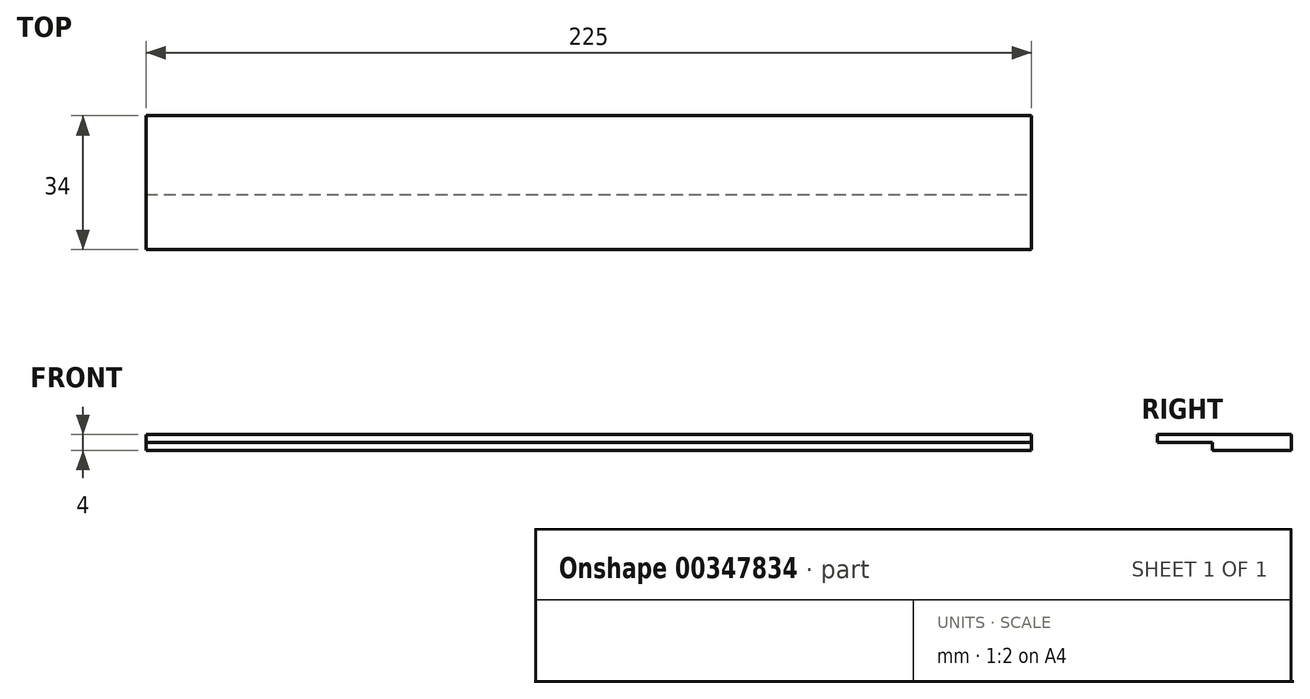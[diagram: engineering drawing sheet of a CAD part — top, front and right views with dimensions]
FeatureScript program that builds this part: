
annotation { "Feature Type Name" : "Feature", "Feature Type Description" : "" }
export const myFeature = defineFeature(function(context is Context, id is Id, definition is map)
    precondition{}
    {
        {
            var Q0;
            Q0=qCreatedBy(makeId("Top.planeOp"),FACE);
            var sketch = newSketch(context, id + "F0", { "sketchPlane" : qUnion([Q0])});
            skLineSegment(sketch, "E0.bottom", {"start": v(112.5, -10) * mm, "end": v(-112.5, -10) * mm});
            skLineSegment(sketch, "E0.top", {"start": v(112.5, 10) * mm, "end": v(-112.5, 10) * mm});
            skLineSegment(sketch, "E0.left", {"start": v(112.5, -10) * mm, "end": v(112.5, 10) * mm});
            skLineSegment(sketch, "E0.right", {"start": v(-112.5, -10) * mm, "end": v(-112.5, 10) * mm});
            skPoint(sketch, "E0.middle", {"position": v(0, 0) * mm});
            skSolve(sketch);
        }
        {
            var Q0;
            Q0 = qSketchRegion(id + "F0", true);
            extrude(context, id + "F1", {"entities" : qUnion([Q0]), "depth" : 2 * mm});
        }
        {
            var Q0;
            Q0=makeQuery(id+"F1.opExtrude","CAP_FACE",FACE,{"disambiguationData":[OSD([sQuery(id+"F0.wireOp",EDGE,"E0.bottom"),sQuery(id+"F0.wireOp",EDGE,"E0.top"),sQuery(id+"F0.wireOp",EDGE,"E0.left"),sQuery(id+"F0.wireOp",EDGE,"E0.right")])],"isStart":false});
            var sketch = newSketch(context, id + "F2", { "sketchPlane" : qUnion([Q0])});
            skPoint(sketch, "E1", {"position": v(-112.5, 4) * mm});
            skLineSegment(sketch, "E2.bottom", {"start": v(-112.5, 4) * mm, "end": v(112.5, 4) * mm});
            skLineSegment(sketch, "E2.top", {"start": v(-112.5, 24) * mm, "end": v(112.5, 24) * mm});
            skLineSegment(sketch, "E2.left", {"start": v(-112.5, 4) * mm, "end": v(-112.5, 24) * mm});
            skLineSegment(sketch, "E2.right", {"start": v(112.5, 4) * mm, "end": v(112.5, 24) * mm});
            skSolve(sketch);
        }
        {
            var Q0;
            {var subQ0=sQuery(id+"F2.wireOp",EDGE,"E2.top");Q0=makeQuery(id+"F2.imprint","IMPRINT",FACE,{"disambiguationData":[TD([[makeQuery(id+"F2.imprint","IMPRINT",EDGE,{"derivedFrom":subQ0}),-1.0]])]});}
            var Q1;
            {var subQ0=sQuery(id+"F2.wireOp",EDGE,"E2.bottom");Q1=makeQuery(id+"F2.imprint","IMPRINT",FACE,{"disambiguationData":[TD([[makeQuery(id+"F2.imprint","IMPRINT",EDGE,{"derivedFrom":subQ0}),1.0]])]});}
            extrude(context, id + "F3", {"entities" : qUnion([Q0, Q1]), "operationType" : NewBodyOperationType.ADD, "oppositeDirection" : true, "depth" : 4 * mm});
        }
    });
